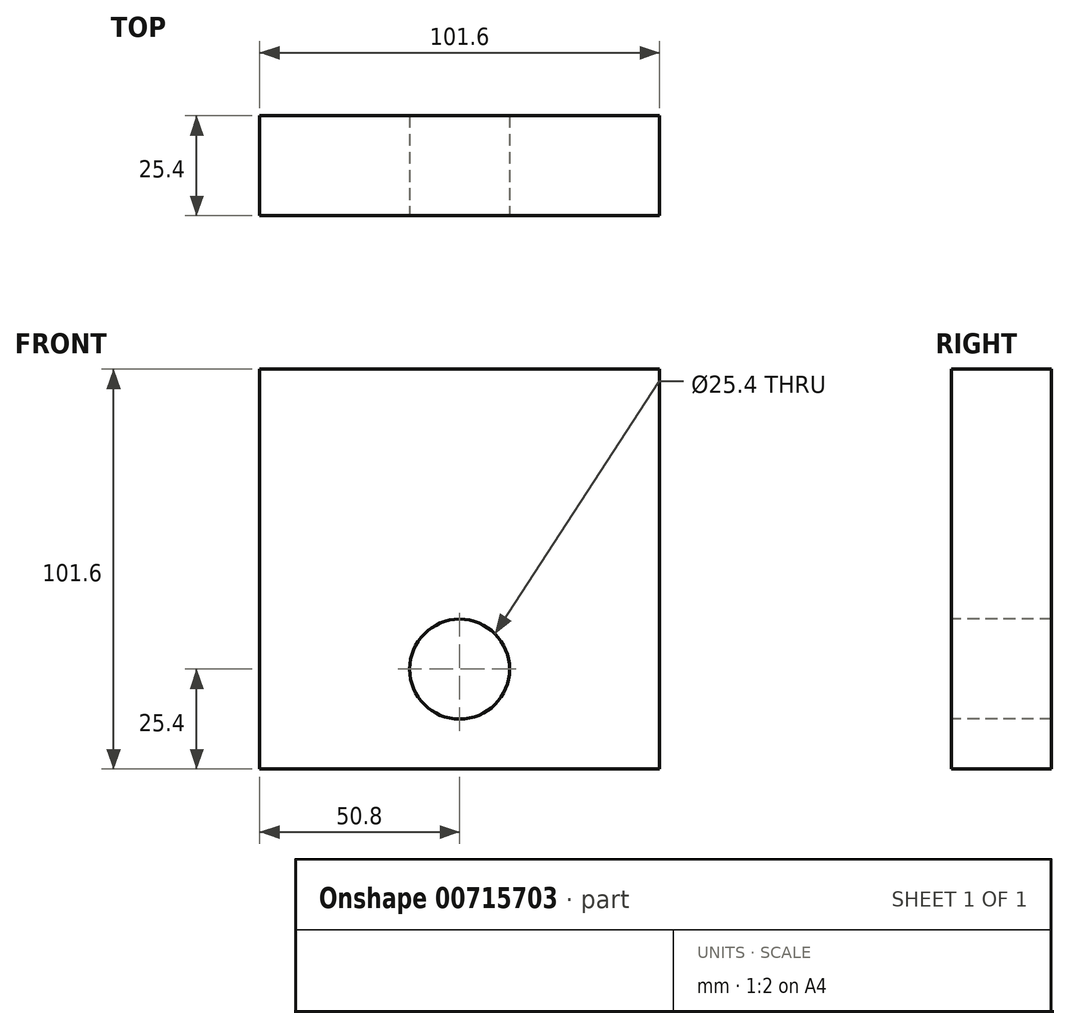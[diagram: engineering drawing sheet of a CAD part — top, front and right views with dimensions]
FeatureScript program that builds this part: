
annotation { "Feature Type Name" : "Feature", "Feature Type Description" : "" }
export const myFeature = defineFeature(function(context is Context, id is Id, definition is map)
    precondition{}
    {
        {
            var Q0;
            Q0=qCreatedBy(makeId("Front.planeOp"),FACE);
            var sketch = newSketch(context, id + "F0", { "sketchPlane" : qUnion([Q0])});
            skLineSegment(sketch, "E0.bottom", {"start": v(0, 101.6) * mm, "end": v(101.6, 101.6) * mm});
            skLineSegment(sketch, "E0.top", {"start": v(0, 0) * mm, "end": v(101.6, 0) * mm});
            skLineSegment(sketch, "E0.left", {"start": v(0, 101.6) * mm, "end": v(0, 0) * mm});
            skLineSegment(sketch, "E0.right", {"start": v(101.6, 101.6) * mm, "end": v(101.6, 0) * mm});
            skSolve(sketch);
        }
        {
            var Q0;
            Q0=makeQuery(id+"F0.imprint","IMPRINT",FACE,{"disambiguationData":[TD([[makeQuery(id+"F0.imprint","IMPRINT",EDGE,{"derivedFrom":sQuery(id+"F0.wireOp",EDGE,"E0.bottom")}),-1.0]])]});
            extrude(context, id + "F1", {"entities" : qUnion([Q0]), "depth" : 25.4 * mm, "offsetDistance" : 25.4 * mm});
        }
        {
            var Q0;
            Q0=makeQuery(id+"F1.opExtrude","CAP_FACE",FACE,{"disambiguationData":[OSD([sQuery(id+"F0.wireOp",EDGE,"E0.bottom"),sQuery(id+"F0.wireOp",EDGE,"E0.top"),sQuery(id+"F0.wireOp",EDGE,"E0.left"),sQuery(id+"F0.wireOp",EDGE,"E0.right")])],"isStart":false});
            var sketch = newSketch(context, id + "F2", { "sketchPlane" : qUnion([Q0])});
            skLineSegment(sketch, "E1", {"start": v(0, 50.8) * mm, "end": v(50.8, 50.8) * mm, "construction": true});
            skLineSegment(sketch, "E2", {"start": v(101.6, 50.8) * mm, "end": v(50.8, 50.8) * mm, "construction": true});
            skLineSegment(sketch, "E3", {"start": v(50.8, 101.6) * mm, "end": v(50.8, 50.8) * mm});
            skLineSegment(sketch, "E4", {"start": v(50.8, 50.8) * mm, "end": v(50.8, 0) * mm});
            skPoint(sketch, "E5", {"position": v(50.8, 25.4) * mm});
            skPoint(sketch, "E6", {"position": v(50.8, 76.2) * mm});
            skCircle(sketch, "E7", {"center": v(50.8, 25.4) * mm, "radius": 12.7 * mm});
            skSolve(sketch);
        }
        {
            var Q0;
            Q0=qSketchRegion(id+"F2",true);
            extrude(context, id + "F3", {"entities" : qUnion([Q0]), "operationType" : NewBodyOperationType.REMOVE, "endBound" : BoundingType.THROUGH_ALL, "oppositeDirection" : true, "depth" : 25.4 * mm, "offsetDistance" : 25.4 * mm});
        }
    });
